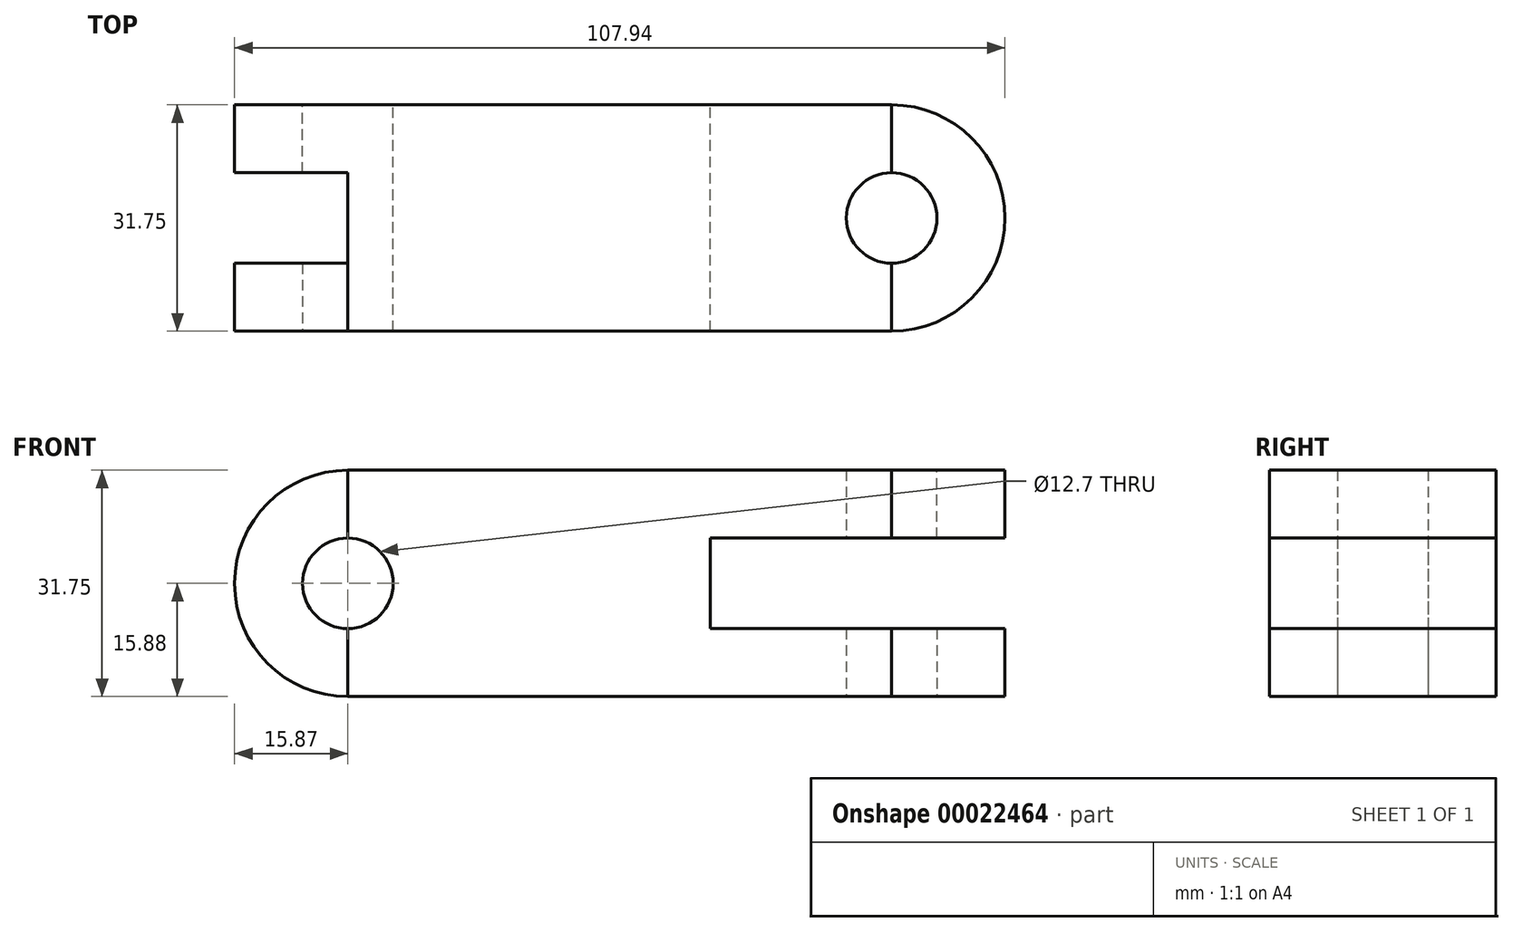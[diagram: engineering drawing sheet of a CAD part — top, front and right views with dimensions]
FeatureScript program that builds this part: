
annotation { "Feature Type Name" : "Feature", "Feature Type Description" : "" }
export const myFeature = defineFeature(function(context is Context, id is Id, definition is map)
    precondition{}
    {
        {
            var Q0;
            Q0=qCreatedBy(makeId("Front.planeOp"),FACE);
            var sketch = newSketch(context, id + "F0", { "sketchPlane" : qUnion([Q0])});
            skLineSegment(sketch, "E0.bottom", {"start": v(-50.8, 34.92) * mm, "end": v(25.4, 34.92) * mm});
            skLineSegment(sketch, "E0.top", {"start": v(-50.8, 3.18) * mm, "end": v(25.4, 3.18) * mm});
            skLineSegment(sketch, "E0.left", {"start": v(-50.8, 34.92) * mm, "end": v(-50.8, 25.4) * mm});
            skLineSegment(sketch, "E1", {"start": v(25.4, 34.92) * mm, "end": v(25.4, 25.4) * mm});
            skLineSegment(sketch, "E2", {"start": v(25.4, 25.4) * mm, "end": v(0, 25.4) * mm});
            skLineSegment(sketch, "E3", {"start": v(0, 25.4) * mm, "end": v(0, 12.7) * mm});
            skLineSegment(sketch, "E4", {"start": v(0, 12.7) * mm, "end": v(25.4, 12.7) * mm});
            skLineSegment(sketch, "E5", {"start": v(25.4, 12.7) * mm, "end": v(25.4, 3.18) * mm});
            skCircle(sketch, "E6", {"center": v(-50.8, 19.05) * mm, "radius": 6.35 * mm});
            skArc(sketch, "E7", {"start": v(-50.8, 34.92) * mm, "mid": v(-66.68, 19.05) * mm, "end": v(-50.8, 3.18) * mm});
            skLineSegment(sketch, "E8.trimOffspring", {"start": v(-50.8, 12.7) * mm, "end": v(-50.8, 3.18) * mm});
            skSolve(sketch);
        }
        {
            var Q0;
            Q0=makeQuery(id+"F0.imprint","IMPRINT",FACE,{"disambiguationData":[TD([[makeQuery(id+"F0.imprint","IMPRINT",EDGE,{"derivedFrom":sQuery(id+"F0.wireOp",EDGE,"E0.bottom")}),-1.0]])]});
            extrude(context, id + "F1", {"entities" : qUnion([Q0]), "depth" : 31.75 * mm});
        }
        {
            var Q0;
            Q0 = qSketchRegion(id + "F0", true);
            extrude(context, id + "F2", {"entities" : qUnion([Q0]), "operationType" : NewBodyOperationType.ADD, "depth" : 9.52 * mm});
        }
        {
            var Q0;
            Q0=makeQuery(id+"F1.opExtrude","CAP_FACE",FACE,{"disambiguationData":[OSD([sQuery(id+"F0.wireOp",EDGE,"E0.bottom"),sQuery(id+"F0.wireOp",EDGE,"E0.top"),sQuery(id+"F0.wireOp",EDGE,"E0.left"),sQuery(id+"F0.wireOp",EDGE,"E1"),sQuery(id+"F0.wireOp",EDGE,"E2"),sQuery(id+"F0.wireOp",EDGE,"E3"),sQuery(id+"F0.wireOp",EDGE,"E4"),sQuery(id+"F0.wireOp",EDGE,"E5"),sQuery(id+"F0.wireOp",EDGE,"E6"),sQuery(id+"F0.wireOp",EDGE,"E8.trimOffspring")])],"isStart":false});
            var sketch = newSketch(context, id + "F3", { "sketchPlane" : qUnion([Q0])});
            skArc(sketch, "E9", {"start": v(-50.8, 34.92) * mm, "mid": v(-66.68, 19.05) * mm, "end": v(-50.8, 3.18) * mm});
            skLineSegment(sketch, "E10", {"start": v(-50.8, 34.92) * mm, "end": v(-50.8, 3.18) * mm, "construction": true});
            skCircle(sketch, "E11", {"center": v(-50.8, 19.05) * mm, "radius": 6.35 * mm});
            skSolve(sketch);
        }
        {
            var Q0;
            Q0=makeQuery(id+"F3.imprint","IMPRINT",FACE,{"disambiguationData":[TD([[makeQuery(id+"F3.imprint","IMPRINT",EDGE,{"derivedFrom":sQuery(id+"F3.wireOp",EDGE,"E9")}),1.0]])]});
            extrude(context, id + "F4", {"entities" : qUnion([Q0]), "oppositeDirection" : true, "depth" : 9.52 * mm});
        }
        {
            var Q0;
            Q0=makeQuery(id+"F1.opExtrude","SWEPT_FACE",FACE,{"disambiguationData":[OSD([sQuery(id+"F0.wireOp",EDGE,"E0.bottom")])]});
            var sketch = newSketch(context, id + "F5", { "sketchPlane" : qUnion([Q0])});
            skCircle(sketch, "E12", {"center": v(25.4, -15.88) * mm, "radius": 6.35 * mm});
            skArc(sketch, "E13", {"start": v(25.4, -31.75) * mm, "mid": v(41.28, -15.88) * mm, "end": v(25.4, 0) * mm});
            skLineSegment(sketch, "E14", {"start": v(25.4, 0) * mm, "end": v(25.4, -31.75) * mm, "construction": true});
            skSolve(sketch);
        }
        {
            var Q0;
            {var subQ4=sQuery(id+"F5.wireOp",EDGE,"E13");Q0=makeQuery(id+"F5.imprint","IMPRINT",FACE,{"disambiguationData":[TD([[makeQuery(id+"F5.imprint","IMPRINT",EDGE,{"derivedFrom":subQ4}),1.0]])]});}
            extrude(context, id + "F6", {"entities" : qUnion([Q0]), "oppositeDirection" : true, "depth" : 9.52 * mm});
        }
        {
            var Q0;
            Q0=makeQuery(id+"F1.opExtrude","SWEPT_FACE",FACE,{"disambiguationData":[OSD([sQuery(id+"F0.wireOp",EDGE,"E0.top")])]});
            var sketch = newSketch(context, id + "F7", { "sketchPlane" : qUnion([Q0])});
            skCircle(sketch, "E15", {"center": v(25.4, 15.88) * mm, "radius": 6.35 * mm});
            skArc(sketch, "E16", {"start": v(25.4, 0) * mm, "mid": v(41.28, 15.87) * mm, "end": v(25.4, 31.75) * mm});
            skLineSegment(sketch, "E17", {"start": v(25.4, 31.75) * mm, "end": v(25.4, 0) * mm, "construction": true});
            skSolve(sketch);
        }
        {
            var Q0;
            {var subQ4=sQuery(id+"F7.wireOp",EDGE,"E16");Q0=makeQuery(id+"F7.imprint","IMPRINT",FACE,{"disambiguationData":[TD([[makeQuery(id+"F7.imprint","IMPRINT",EDGE,{"derivedFrom":subQ4}),1.0]])]});}
            extrude(context, id + "F8", {"entities" : qUnion([Q0]), "oppositeDirection" : true, "depth" : 9.52 * mm});
        }
        {
            var Q0;
            Q0=makeQuery(id+"F1.opExtrude","SWEPT_FACE",FACE,{"disambiguationData":[OSD([sQuery(id+"F0.wireOp",EDGE,"E0.top")])]});
            var sketch = newSketch(context, id + "F9", { "sketchPlane" : qUnion([Q0])});
            skCircle(sketch, "E18", {"center": v(25.4, 15.88) * mm, "radius": 6.35 * mm});
            skSolve(sketch);
        }
        {
            var Q0;
            {var subQ0=makeQuery(id+"F1.opExtrude","SWEPT_EDGE",EDGE,{"disambiguationData":[OSD([sQuery(id+"F0.wireOp",EDGE,"E0.top"),sQuery(id+"F0.wireOp",EDGE,"E5")])]});var subQ1=sQuery(id+"F9.wireOp",EDGE,"E18");var subQ3=makeQuery(id+"F9.imprint","INTERSECT",VERTEX,{"disambiguationData":[OD(0.0)],"derivedFrom":[subQ0,subQ1]});Q0=makeQuery(id+"F9.imprint","IMPRINT",FACE,{"disambiguationData":[TD([[makeQuery(id+"F9.imprint","IMPRINT",EDGE,{"disambiguationData":[TD([[subQ3,-1.0]])],"derivedFrom":subQ1}),1.0]])]});}
            var Q1;
            {var subQ0=makeQuery(id+"F1.opExtrude","SWEPT_EDGE",EDGE,{"disambiguationData":[OSD([sQuery(id+"F0.wireOp",EDGE,"E0.top"),sQuery(id+"F0.wireOp",EDGE,"E5")])]});var subQ1=sQuery(id+"F9.wireOp",EDGE,"E18");var subQ3=makeQuery(id+"F9.imprint","INTERSECT",VERTEX,{"disambiguationData":[OD(0.0)],"derivedFrom":[subQ0,subQ1]});Q1=makeQuery(id+"F9.imprint","IMPRINT",FACE,{"disambiguationData":[TD([[makeQuery(id+"F9.imprint","IMPRINT",EDGE,{"disambiguationData":[TD([[subQ3,1.0]])],"derivedFrom":subQ1}),1.0]])]});}
            extrude(context, id + "F10", {"entities" : qUnion([Q0, Q1]), "operationType" : NewBodyOperationType.REMOVE, "oppositeDirection" : true, "depth" : 25.4 * mm});
        }
        {
            var Q0;
            Q0=makeQuery(id+"F1.opExtrude","SWEPT_FACE",FACE,{"disambiguationData":[OSD([sQuery(id+"F0.wireOp",EDGE,"E0.bottom")])]});
            var sketch = newSketch(context, id + "F11", { "sketchPlane" : qUnion([Q0])});
            skCircle(sketch, "E19", {"center": v(25.4, -15.88) * mm, "radius": 6.35 * mm});
            skSolve(sketch);
        }
        {
            var Q0;
            Q0 = qSketchRegion(id + "F11", true);
            extrude(context, id + "F12", {"entities" : qUnion([Q0]), "operationType" : NewBodyOperationType.REMOVE, "oppositeDirection" : true, "depth" : 25.4 * mm});
        }
    });
